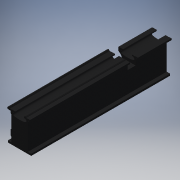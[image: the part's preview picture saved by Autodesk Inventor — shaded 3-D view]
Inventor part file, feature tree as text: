
AUTODESK INVENTOR PART (.ipt)
format: ipt  version: 2016 (Build 200138000, 138)  size: 403,968 bytes
history: native  units: in
note: dims shown in document units (in); Inventor stores cm internally (conversion verified against a paired STEP export)
features: extrude x11, sketch x11, reference x6, plane x3, chamfer x1
ambient origin geometry x8: Origin, YZ Plane, XZ Plane, XY Plane, X Axis, Y Axis, Z Axis, Center Point
bodies: Solid1 (feature_tree)
feature tree (32):
  extrude  "Extrusion1"  TaperAngle=150.0deg  [1 undecoded]
  chamfer  "Chamfer1"  Distance=0.9921in
  plane  "Work Plane3"
  extrude  "Extrusion2"  Depth=0.5118in
  extrude  "Extrusion3"  Depth=0.5118in
  extrude  "Extrusion4"  Depth=0.5118in
  extrude  "Extrusion5"  TaperAngle=120.0deg  [1 undecoded]
  extrude  "Extrusion6"  Depth=0.1575in
  extrude  "Extrusion7"  Depth=0.5118in
  extrude  "Extrusion8"  Depth=0.5118in
  plane  "Work Plane4"
  plane  "Work Plane5"
  extrude  "Extrusion9"  Depth=0.5118in
  extrude  "Extrusion10"  Depth=0.5118in
  extrude  "Extrusion11"  Depth=0.5118in
  sketch  "Sketch1"  dims[d0=0.4331in d1=150.0deg]
  sketch  "Sketch2"  dims[d2=0.3937in]
  sketch  "Sketch3"  dims[d3=0.4606in]
  sketch  "Sketch4"  dims[d4=0.4961in]
  sketch  "Sketch5"  dims[d5=0.962in]
  sketch  "Sketch6"  dims[d6=0.1496in]
  sketch  "Sketch8"  dims[d7=0.4016in]
  sketch  "Sketch9"  dims[d8=0.962in]
  sketch  "Sketch10"  dims[d9=0.126in]
  sketch  "Sketch11"  dims[d10=0.6339in]
  sketch  "Sketch12"  dims[d11=0.0787in d12=0.9921in d13=0.6181in d14=0.5787in d15=0.315in d16=120.0deg d17=0.1575in d18=2.4409in d19=8.0315in d22=3.6299in d24=0.5in d25=1.4252in d26=180.0deg d27=0.0787in d28=0.748in d29=0.0787in d30=0.5197in d31=0.962in d32=0.1811in d33=0.6299in d34=0.962in d35=0.5512in d36=0.5512in d37=90.0deg d38=0.1181in d39=60.0deg d40=0.685in d41=0.8858in d43=5.2953in d44=90.0deg d46=2.185in d47=90.0deg d50=90.0deg d51=1.378in d52=180.0deg d53=0.7087in d54=90.0deg d55=1.378in d57=0.7087in d59=180.0deg d60=0.315in d61=120.0deg d62=2.4409in d63=55.9055in d64=0.0in d65=0.1575in d66=0.0787in d67=45.0deg d68=40.1575in d69=3.2283in d70=3.4528in d71=55.9055in d72=0.0in d73=55.9055in d74=0.0in d75=55.9055in d76=0.0in d77=3.3465in d78=1.2205in d79=1.7323in d80=55.9055in d81=0.0in d82=1.0236in d83=0.0in d84=0.315in d85=0.315in d86=0.7283in d87=0.5512in d88=0.5118in d89=0.3937in d90=0.0in d91=0.315in d92=0.315in d93=6.7717in d94=0.9449in d95=0.5512in d96=0.7874in d97=0.0in d98=0.2756in d99=0.3937in d100=0.0in d101=5.5118in d102=1.9685in d103=0.2756in d104=1.5748in d105=0.0787in d106=0.0in d107=0.7874in d108=0.0in d109=0.0787in d110=0.3937in d111=1.2205in d112=0.2362in d113=0.2362in d114=1.0236in d116=0.5118in d117=3.189in]
  reference  "Reference1"
  reference  "Reference2"
  reference  "Reference3"
  reference  "Reference4"
  reference  "Reference5"
  reference  "Reference6"
note: 2 required parameter values undecoded (feature->parameter linkage not recoverable at this tier; creation-order binding heuristic only, values carry confidence <= 0.55)
